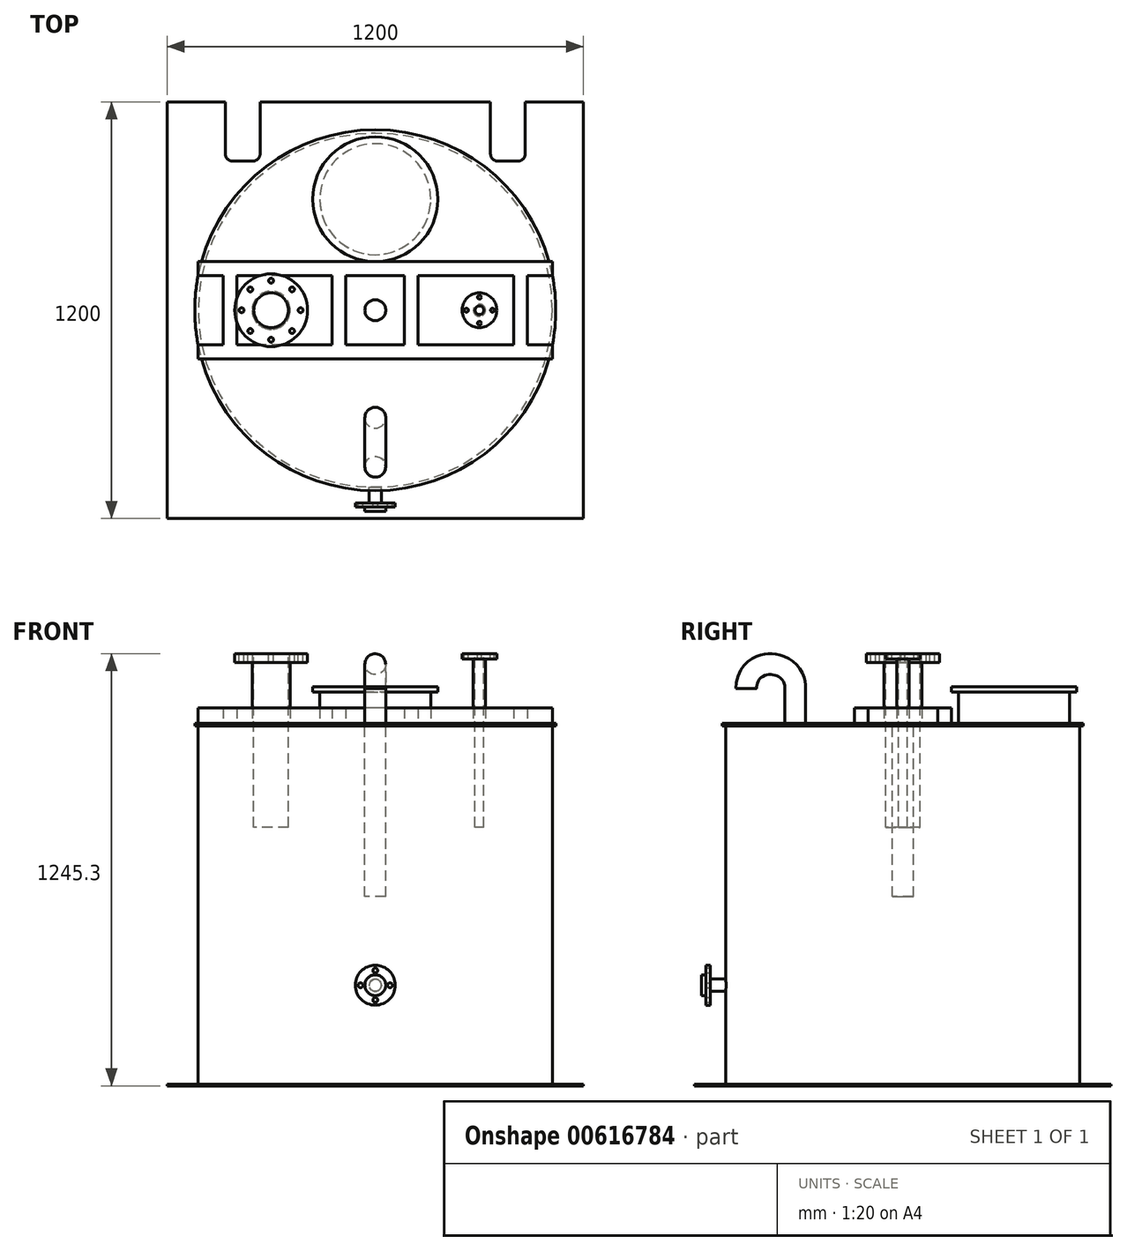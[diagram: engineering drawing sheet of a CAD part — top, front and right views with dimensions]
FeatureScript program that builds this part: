
annotation { "Feature Type Name" : "Feature", "Feature Type Description" : "" }
export const myFeature = defineFeature(function(context is Context, id is Id, definition is map)
    precondition{}
    {
        {
            var Q0;
            Q0=qCreatedBy(makeId("Front.planeOp"),FACE);
            var sketch = newSketch(context, id + "F0", { "sketchPlane" : qUnion([Q0])});
            skLineSegment(sketch, "E0.bottom", {"start": v(0, 0) * mm, "end": v(510, 0) * mm});
            skLineSegment(sketch, "E0.top", {"start": v(0, 1040) * mm, "end": v(510, 1040) * mm});
            skLineSegment(sketch, "E0.left", {"start": v(0, 0) * mm, "end": v(0, 1040) * mm});
            skLineSegment(sketch, "E0.right", {"start": v(510, 0) * mm, "end": v(510, 1032) * mm});
            skLineSegment(sketch, "E1.bottom", {"start": v(510, 1040) * mm, "end": v(520, 1040) * mm});
            skLineSegment(sketch, "E1.top", {"start": v(510, 1032) * mm, "end": v(520, 1032) * mm});
            skLineSegment(sketch, "E1.right", {"start": v(520, 1040) * mm, "end": v(520, 1032) * mm});
            skSolve(sketch);
        }
        {
            var Q0;
            Q0=makeQuery(id+"F0.imprint","IMPRINT",FACE,{"disambiguationData":[TD([[makeQuery(id+"F0.imprint","IMPRINT",EDGE,{"derivedFrom":sQuery(id+"F0.wireOp",EDGE,"E0.bottom")}),1.0]])]});
            var Q1;
            Q1=sQuery(id+"F0.wireOp",EDGE,"E0.left");
            revolve(context, id + "F1", {"entities" : qUnion([Q0]), "axis" : qUnion([Q1]), "revolveType" : RevolveType.FULL});
        }
        {
            var Q0;
            Q0=makeQuery(id+"F1.opRevolve","SWEPT_FACE",FACE,{"disambiguationData":[OSD([sQuery(id+"F0.wireOp",EDGE,"E0.bottom")])]});
            var sketch = newSketch(context, id + "F2", { "sketchPlane" : qUnion([Q0])});
            skLineSegment(sketch, "E2.bottom", {"start": v(600, -600) * mm, "end": v(432, -600) * mm});
            skLineSegment(sketch, "E2.top", {"start": v(600, 600) * mm, "end": v(-600, 600) * mm});
            skLineSegment(sketch, "E2.left", {"start": v(600, -600) * mm, "end": v(600, 600) * mm});
            skLineSegment(sketch, "E2.right", {"start": v(-600, -600) * mm, "end": v(-600, 600) * mm});
            skPoint(sketch, "E2.middle", {"position": v(0, 0) * mm});
            skLineSegment(sketch, "E3.top", {"start": v(412, -430) * mm, "end": v(352, -430) * mm});
            skLineSegment(sketch, "E3.left", {"start": v(332, -600) * mm, "end": v(332, -450) * mm});
            skLineSegment(sketch, "E3.right", {"start": v(432, -600) * mm, "end": v(432, -450) * mm});
            skLineSegment(sketch, "E4.top", {"start": v(-352, -430) * mm, "end": v(-412, -430) * mm});
            skLineSegment(sketch, "E4.left", {"start": v(-332, -600) * mm, "end": v(-332, -450) * mm});
            skLineSegment(sketch, "E4.right", {"start": v(-432, -600) * mm, "end": v(-432, -450) * mm});
            skPoint(sketch, "E5.visualSharp", {"position": v(-432, -430) * mm});
            skArc(sketch, "E5.filletArc", {"start": v(-412, -430) * mm, "mid": v(-426.14, -435.86) * mm, "end": v(-432, -450) * mm});
            skPoint(sketch, "E6.visualSharp", {"position": v(-332, -430) * mm});
            skArc(sketch, "E6.filletArc", {"start": v(-332, -450) * mm, "mid": v(-337.86, -435.86) * mm, "end": v(-352, -430) * mm});
            skPoint(sketch, "E7.visualSharp", {"position": v(332, -430) * mm});
            skArc(sketch, "E7.filletArc", {"start": v(352, -430) * mm, "mid": v(337.86, -435.86) * mm, "end": v(332, -450) * mm});
            skPoint(sketch, "E8.visualSharp", {"position": v(432, -430) * mm});
            skArc(sketch, "E8.filletArc", {"start": v(432, -450) * mm, "mid": v(426.14, -435.86) * mm, "end": v(412, -430) * mm});
            skLineSegment(sketch, "E9.trimOffspring", {"start": v(332, -600) * mm, "end": v(-332, -600) * mm});
            skLineSegment(sketch, "E10.trimOffspring", {"start": v(-432, -600) * mm, "end": v(-600, -600) * mm});
            skSolve(sketch);
        }
        {
            var Q0;
            Q0 = qSketchRegion(id + "F2", true);
            extrude(context, id + "F3", {"entities" : qUnion([Q0]), "operationType" : NewBodyOperationType.ADD, "depth" : 5 * mm, "offsetDistance" : 25 * mm});
        }
        {
            var Q0;
            Q0=qCreatedBy(makeId("Front.planeOp"),FACE);
            var sketch = newSketch(context, id + "F4", { "sketchPlane" : qUnion([Q0])});
            skCircle(sketch, "E11", {"center": v(0, 285) * mm, "radius": 17.5 * mm});
            skSolve(sketch);
        }
        {
            var Q0;
            Q0 = qSketchRegion(id + "F4", true);
            extrude(context, id + "F5", {"entities" : qUnion([Q0]), "operationType" : NewBodyOperationType.ADD, "depth" : 580 * mm, "offsetDistance" : 25 * mm});
        }
        {
            var Q0;
            Q0=makeQuery(id+"F5.opExtrude","CAP_FACE",FACE,{"disambiguationData":[OSD([sQuery(id+"F4.wireOp",EDGE,"E11")])],"isStart":false});
            cPlane(context, id + "F6", {"entities" : qUnion([Q0]), "cplaneType" : CPlaneType.OFFSET, "offset" : 25 * mm, "oppositeDirection" : true, "width" : 150 * mm, "height" : 150 * mm});
        }
        {
            var Q0;
            Q0=qCreatedBy(id+"F6.planeOp",FACE);
            var sketch = newSketch(context, id + "F7", { "sketchPlane" : qUnion([Q0])});
            skCircle(sketch, "E12", {"center": v(0, 285) * mm, "radius": 57.5 * mm});
            skCircle(sketch, "E13", {"center": v(0, 327.5) * mm, "radius": 7 * mm});
            skCircle(sketch, "E14.1.0", {"center": v(-42.5, 285) * mm, "radius": 7 * mm});
            skCircle(sketch, "E14.2.0", {"center": v(0, 242.5) * mm, "radius": 7 * mm});
            skCircle(sketch, "E14.3.0", {"center": v(42.5, 285) * mm, "radius": 7 * mm});
            skSolve(sketch);
        }
        {
            var Q0;
            Q0 = qSketchRegion(id + "F7", true);
            extrude(context, id + "F8", {"entities" : qUnion([Q0]), "operationType" : NewBodyOperationType.ADD, "depth" : 12 * mm, "offsetDistance" : 25 * mm});
        }
        {
            var Q0;
            Q0=makeQuery(id+"F8.opExtrude","CAP_FACE",FACE,{"disambiguationData":[OSD([sQuery(id+"F7.wireOp",EDGE,"E12"),sQuery(id+"F7.wireOp",EDGE,"E13"),sQuery(id+"F7.wireOp",EDGE,"E14.1.0"),sQuery(id+"F7.wireOp",EDGE,"E14.2.0"),sQuery(id+"F7.wireOp",EDGE,"E14.3.0")])],"isStart":false});
            var sketch = newSketch(context, id + "F9", { "sketchPlane" : qUnion([Q0])});
            skCircle(sketch, "E15", {"center": v(0, 285) * mm, "radius": 30 * mm});
            skSolve(sketch);
        }
        {
            var Q0;
            Q0 = qSketchRegion(id + "F9", true);
            extrude(context, id + "F10", {"entities" : qUnion([Q0]), "operationType" : NewBodyOperationType.ADD, "depth" : 13 * mm, "offsetDistance" : 25 * mm});
        }
        {
            var Q0;
            Q0=makeQuery(id+"F1.opRevolve","SWEPT_FACE",FACE,{"disambiguationData":[OSD([sQuery(id+"F0.wireOp",EDGE,"E0.top"),sQuery(id+"F0.wireOp",EDGE,"E1.bottom")])]});
            var sketch = newSketch(context, id + "F11", { "sketchPlane" : qUnion([Q0])});
            skLineSegment(sketch, "E16.bottom", {"start": v(510.5, 140) * mm, "end": v(-510.5, 140) * mm});
            skLineSegment(sketch, "E16.top", {"start": v(510.5, 100) * mm, "end": v(438.5, 100) * mm});
            skLineSegment(sketch, "E16.left", {"start": v(510.5, 140) * mm, "end": v(510.5, 100) * mm});
            skLineSegment(sketch, "E16.right", {"start": v(-510.5, 140) * mm, "end": v(-510.5, 100) * mm});
            skLineSegment(sketch, "E17.bottom", {"start": v(510.5, -100) * mm, "end": v(438.5, -100) * mm});
            skLineSegment(sketch, "E17.top", {"start": v(510.5, -140) * mm, "end": v(-510.5, -140) * mm});
            skLineSegment(sketch, "E17.left", {"start": v(510.5, -100) * mm, "end": v(510.5, -140) * mm});
            skLineSegment(sketch, "E17.right", {"start": v(-510.5, -100) * mm, "end": v(-510.5, -140) * mm});
            skLineSegment(sketch, "E18.left", {"start": v(438.5, 100) * mm, "end": v(438.5, -100) * mm});
            skLineSegment(sketch, "E18.right", {"start": v(398.5, 100) * mm, "end": v(398.5, -100) * mm});
            skLineSegment(sketch, "E19.left", {"start": v(123.5, 100) * mm, "end": v(123.5, -100) * mm});
            skLineSegment(sketch, "E19.right", {"start": v(83.5, 100) * mm, "end": v(83.5, -100) * mm});
            skLineSegment(sketch, "E20.left", {"start": v(-85, 100) * mm, "end": v(-85, -100) * mm});
            skLineSegment(sketch, "E20.right", {"start": v(-125, 100) * mm, "end": v(-125, -100) * mm});
            skLineSegment(sketch, "E21.left", {"start": v(-398.5, 100) * mm, "end": v(-398.5, -100) * mm});
            skLineSegment(sketch, "E21.right", {"start": v(-438.5, 100) * mm, "end": v(-438.5, -100) * mm});
            skLineSegment(sketch, "E22.trimOffspring", {"start": v(398.5, 100) * mm, "end": v(123.5, 100) * mm});
            skLineSegment(sketch, "E23.trimOffspring", {"start": v(83.5, 100) * mm, "end": v(-85, 100) * mm});
            skLineSegment(sketch, "E24.trimOffspring", {"start": v(83.5, -100) * mm, "end": v(-85, -100) * mm});
            skLineSegment(sketch, "E25.trimOffspring", {"start": v(-125, -100) * mm, "end": v(-398.5, -100) * mm});
            skLineSegment(sketch, "E26.trimOffspring", {"start": v(-125, 100) * mm, "end": v(-398.5, 100) * mm});
            skLineSegment(sketch, "E27.trimOffspring", {"start": v(-438.5, 100) * mm, "end": v(-510.5, 100) * mm});
            skLineSegment(sketch, "E28.trimOffspring", {"start": v(-438.5, -100) * mm, "end": v(-510.5, -100) * mm});
            skLineSegment(sketch, "E29", {"start": v(398.5, -100) * mm, "end": v(123.5, -100) * mm});
            skSolve(sketch);
        }
        {
            var Q0;
            Q0 = qSketchRegion(id + "F11", true);
            extrude(context, id + "F12", {"entities" : qUnion([Q0]), "operationType" : NewBodyOperationType.ADD, "depth" : 44 * mm, "offsetDistance" : 25 * mm});
        }
        {
            var Q0;
            {var subQ0=sQuery(id+"F11.wireOp",EDGE,"E16.bottom");Q0=makeQuery(id+"F12.boolean.opBoolean","SPLIT",FACE,{"disambiguationData":[TD([makeQuery(id+"F12.opExtrude","SWEPT_FACE",FACE,{"disambiguationData":[OSD([subQ0])]})])],"derivedFrom":makeQuery(id+"F1.opRevolve","SWEPT_FACE",FACE,{"disambiguationData":[OSD([sQuery(id+"F0.wireOp",EDGE,"E0.top"),sQuery(id+"F0.wireOp",EDGE,"E1.bottom")])]})});}
            var sketch = newSketch(context, id + "F13", { "sketchPlane" : qUnion([Q0])});
            skCircle(sketch, "E30", {"center": v(0, 320) * mm, "radius": 160 * mm});
            skSolve(sketch);
        }
        {
            var Q0;
            Q0=makeQuery(id+"F13.imprint","IMPRINT",FACE,{"disambiguationData":[TD([[makeQuery(id+"F13.imprint","IMPRINT",EDGE,{"derivedFrom":sQuery(id+"F13.wireOp",EDGE,"E30")}),1.0]])]});
            extrude(context, id + "F14", {"entities" : qUnion([Q0]), "operationType" : NewBodyOperationType.ADD, "depth" : 90 * mm, "offsetDistance" : 25 * mm});
        }
        {
            var Q0;
            Q0=makeQuery(id+"F14.opExtrude","CAP_FACE",FACE,{"disambiguationData":[OSD([sQuery(id+"F13.wireOp",EDGE,"E30")])],"isStart":false});
            var sketch = newSketch(context, id + "F15", { "sketchPlane" : qUnion([Q0])});
            skCircle(sketch, "E31", {"center": v(0, 320) * mm, "radius": 180 * mm});
            skSolve(sketch);
        }
        {
            var Q0;
            Q0 = qSketchRegion(id + "F15", true);
            extrude(context, id + "F16", {"entities" : qUnion([Q0]), "operationType" : NewBodyOperationType.ADD, "depth" : 15 * mm, "offsetDistance" : 25 * mm});
        }
        {
            var Q0;
            Q0=makeQuery(id+"F12.boolean.opBoolean","SPLIT",FACE,{"disambiguationData":[TD([makeQuery(id+"F12.opExtrude","SWEPT_FACE",FACE,{"disambiguationData":[OSD([sQuery(id+"F11.wireOp",EDGE,"E19.right")])]})])],"derivedFrom":makeQuery(id+"F1.opRevolve","SWEPT_FACE",FACE,{"disambiguationData":[OSD([sQuery(id+"F0.wireOp",EDGE,"E0.top"),sQuery(id+"F0.wireOp",EDGE,"E1.bottom")])]})});
            var sketch = newSketch(context, id + "F17", { "sketchPlane" : qUnion([Q0])});
            skCircle(sketch, "E32", {"center": v(0, 0) * mm, "radius": 30 * mm});
            skSolve(sketch);
        }
        {
            var Q0;
            Q0=makeQuery(id+"F17.imprint","IMPRINT",FACE,{"disambiguationData":[TD([[makeQuery(id+"F17.imprint","IMPRINT",EDGE,{"derivedFrom":sQuery(id+"F17.wireOp",EDGE,"E32")}),1.0]])]});
            extrude(context, id + "F18", {"entities" : qUnion([Q0]), "operationType" : NewBodyOperationType.REMOVE, "oppositeDirection" : true, "depth" : 500 * mm, "offsetDistance" : 25 * mm});
        }
        {
            var Q0;
            {var subQ0=sQuery(id+"F11.wireOp",EDGE,"E17.top");Q0=makeQuery(id+"F12.boolean.opBoolean","SPLIT",FACE,{"disambiguationData":[TD([makeQuery(id+"F12.opExtrude","SWEPT_FACE",FACE,{"disambiguationData":[OSD([subQ0])]})])],"derivedFrom":makeQuery(id+"F1.opRevolve","SWEPT_FACE",FACE,{"disambiguationData":[OSD([sQuery(id+"F0.wireOp",EDGE,"E0.top"),sQuery(id+"F0.wireOp",EDGE,"E1.bottom")])]})});}
            var sketch = newSketch(context, id + "F19", { "sketchPlane" : qUnion([Q0])});
            skCircle(sketch, "E33", {"center": v(0, -310) * mm, "radius": 30 * mm});
            skSolve(sketch);
        }
        {
            var Q0;
            Q0=qCreatedBy(makeId("Right.planeOp"),FACE);
            var sketch = newSketch(context, id + "F20", { "sketchPlane" : qUnion([Q0])});
            skPoint(sketch, "E34.0", {"position": v(-310, 1040) * mm});
            skLineSegment(sketch, "E35", {"start": v(-310, 1040) * mm, "end": v(-310, 1140) * mm});
            skFitSpline(sketch, "E36", {"points": [v(-310, 1140) * mm, v(-451.09, 1140) * mm], "startDerivative": vector(-1.84, 276.58) * mm, "endDerivative": vector(1.84, -285.78) * mm});
            skSolve(sketch);
        }
        {
            var Q0;
            Q0=makeQuery(id+"F19.imprint","IMPRINT",FACE,{"disambiguationData":[TD([[makeQuery(id+"F19.imprint","IMPRINT",EDGE,{"derivedFrom":sQuery(id+"F19.wireOp",EDGE,"E33")}),1.0]])]});
            var Q1;
            Q1=sQuery(id+"F20.wireOp",EDGE,"E35");
            var Q2;
            Q2=sQuery(id+"F20.wireOp",EDGE,"E36");
            sweep(context, id + "F21", {"operationType" : NewBodyOperationType.ADD, "profiles" : qUnion([Q0]), "path" : qUnion([Q1, Q2])});
        }
        {
            var Q0;
            Q0=makeQuery(id+"F12.boolean.opBoolean","SPLIT",FACE,{"disambiguationData":[TD([makeQuery(id+"F12.opExtrude","SWEPT_FACE",FACE,{"disambiguationData":[OSD([sQuery(id+"F11.wireOp",EDGE,"E20.right")])]})])],"derivedFrom":makeQuery(id+"F1.opRevolve","SWEPT_FACE",FACE,{"disambiguationData":[OSD([sQuery(id+"F0.wireOp",EDGE,"E0.top"),sQuery(id+"F0.wireOp",EDGE,"E1.bottom")])]})});
            var sketch = newSketch(context, id + "F22", { "sketchPlane" : qUnion([Q0])});
            skCircle(sketch, "E37", {"center": v(300, 0) * mm, "radius": 17.5 * mm});
            skCircle(sketch, "E38", {"center": v(-300, 0) * mm, "radius": 55 * mm});
            skSolve(sketch);
        }
        {
            var Q0;
            Q0 = qSketchRegion(id + "F22", true);
            extrude(context, id + "F23", {"entities" : qUnion([Q0]), "operationType" : NewBodyOperationType.ADD, "depth" : 200 * mm, "offsetDistance" : 25 * mm});
        }
        {
            var Q0;
            Q0=makeQuery(id+"F23.opExtrude","CAP_FACE",FACE,{"disambiguationData":[OSD([sQuery(id+"F22.wireOp",EDGE,"E38")])],"isStart":false});
            var sketch = newSketch(context, id + "F24", { "sketchPlane" : qUnion([Q0])});
            skCircle(sketch, "E39", {"center": v(-300, 0) * mm, "radius": 105 * mm});
            skCircle(sketch, "E40", {"center": v(-215, 0) * mm, "radius": 7 * mm});
            skCircle(sketch, "E41.1.0", {"center": v(-239.9, 60.1) * mm, "radius": 7 * mm});
            skCircle(sketch, "E41.2.0", {"center": v(-300, 85) * mm, "radius": 7 * mm});
            skCircle(sketch, "E41.3.0", {"center": v(-360.1, 60.1) * mm, "radius": 7 * mm});
            skCircle(sketch, "E41.4.0", {"center": v(-385, 0) * mm, "radius": 7 * mm});
            skCircle(sketch, "E41.5.0", {"center": v(-360.1, -60.1) * mm, "radius": 7 * mm});
            skCircle(sketch, "E41.6.0", {"center": v(-300, -85) * mm, "radius": 7 * mm});
            skCircle(sketch, "E41.7.0", {"center": v(-239.9, -60.1) * mm, "radius": 7 * mm});
            skSolve(sketch);
        }
        {
            var Q0;
            Q0 = qSketchRegion(id + "F24", true);
            extrude(context, id + "F25", {"entities" : qUnion([Q0]), "operationType" : NewBodyOperationType.ADD, "oppositeDirection" : true, "depth" : 25 * mm, "offsetDistance" : 25 * mm});
        }
        {
            var Q0;
            Q0=makeQuery(id+"F25.boolean.opBoolean","MERGE",FACE,{"derivedFrom":[makeQuery(id+"F23.opExtrude","CAP_FACE",FACE,{"disambiguationData":[OSD([sQuery(id+"F22.wireOp",EDGE,"E38")])],"isStart":false}),makeQuery(id+"F25.opExtrude","CAP_FACE",FACE,{"disambiguationData":[OSD([sQuery(id+"F24.wireOp",EDGE,"E39"),sQuery(id+"F24.wireOp",EDGE,"E40"),sQuery(id+"F24.wireOp",EDGE,"E41.1.0"),sQuery(id+"F24.wireOp",EDGE,"E41.2.0"),sQuery(id+"F24.wireOp",EDGE,"E41.3.0"),sQuery(id+"F24.wireOp",EDGE,"E41.4.0"),sQuery(id+"F24.wireOp",EDGE,"E41.5.0"),sQuery(id+"F24.wireOp",EDGE,"E41.6.0"),sQuery(id+"F24.wireOp",EDGE,"E41.7.0")])],"isStart":true})]});
            var sketch = newSketch(context, id + "F26", { "sketchPlane" : qUnion([Q0])});
            skCircle(sketch, "E42", {"center": v(-300, 0) * mm, "radius": 50 * mm});
            skSolve(sketch);
        }
        {
            var Q0;
            Q0=makeQuery(id+"F26.imprint","IMPRINT",FACE,{"disambiguationData":[TD([[makeQuery(id+"F26.imprint","IMPRINT",EDGE,{"derivedFrom":sQuery(id+"F26.wireOp",EDGE,"E42")}),1.0]])]});
            extrude(context, id + "F27", {"entities" : qUnion([Q0]), "operationType" : NewBodyOperationType.REMOVE, "oppositeDirection" : true, "depth" : 500 * mm, "offsetDistance" : 25 * mm});
        }
        {
            var Q0;
            Q0=makeQuery(id+"F23.opExtrude","CAP_FACE",FACE,{"disambiguationData":[OSD([sQuery(id+"F22.wireOp",EDGE,"E37")])],"isStart":false});
            var sketch = newSketch(context, id + "F28", { "sketchPlane" : qUnion([Q0])});
            skCircle(sketch, "E43", {"center": v(300, 0) * mm, "radius": 50 * mm});
            skSolve(sketch);
        }
        {
            var Q0;
            Q0 = qSketchRegion(id + "F28", true);
            extrude(context, id + "F29", {"entities" : qUnion([Q0]), "operationType" : NewBodyOperationType.ADD, "oppositeDirection" : true, "depth" : 15 * mm, "offsetDistance" : 25 * mm});
        }
        {
            var Q0;
            Q0=makeQuery(id+"F29.boolean.opBoolean","MERGE",FACE,{"derivedFrom":[makeQuery(id+"F23.opExtrude","CAP_FACE",FACE,{"disambiguationData":[OSD([sQuery(id+"F22.wireOp",EDGE,"E37")])],"isStart":false}),makeQuery(id+"F29.opExtrude","CAP_FACE",FACE,{"disambiguationData":[OSD([sQuery(id+"F28.wireOp",EDGE,"E43")])],"isStart":true})]});
            var sketch = newSketch(context, id + "F30", { "sketchPlane" : qUnion([Q0])});
            skCircle(sketch, "E44", {"center": v(337.5, 0) * mm, "radius": 5.5 * mm});
            skCircle(sketch, "E45.1.0", {"center": v(300, 37.5) * mm, "radius": 5.5 * mm});
            skCircle(sketch, "E45.2.0", {"center": v(262.5, 0) * mm, "radius": 5.5 * mm});
            skCircle(sketch, "E45.3.0", {"center": v(300, -37.5) * mm, "radius": 5.5 * mm});
            skPoint(sketch, "E45.center", {"position": v(300, 0) * mm});
            skSolve(sketch);
        }
        {
            var Q0;
            Q0 = qSketchRegion(id + "F30", true);
            extrude(context, id + "F31", {"entities" : qUnion([Q0]), "operationType" : NewBodyOperationType.REMOVE, "oppositeDirection" : true, "depth" : 25 * mm, "offsetDistance" : 25 * mm});
        }
        {
            var Q0;
            Q0=makeQuery(id+"F29.boolean.opBoolean","MERGE",FACE,{"derivedFrom":[makeQuery(id+"F23.opExtrude","CAP_FACE",FACE,{"disambiguationData":[OSD([sQuery(id+"F22.wireOp",EDGE,"E37")])],"isStart":false}),makeQuery(id+"F29.opExtrude","CAP_FACE",FACE,{"disambiguationData":[OSD([sQuery(id+"F28.wireOp",EDGE,"E43")])],"isStart":true})]});
            var sketch = newSketch(context, id + "F32", { "sketchPlane" : qUnion([Q0])});
            skCircle(sketch, "E46", {"center": v(300, 0) * mm, "radius": 12.5 * mm});
            skSolve(sketch);
        }
        {
            var Q0;
            Q0=makeQuery(id+"F32.imprint","IMPRINT",FACE,{"disambiguationData":[TD([[makeQuery(id+"F32.imprint","IMPRINT",EDGE,{"derivedFrom":sQuery(id+"F32.wireOp",EDGE,"E46")}),1.0]])]});
            extrude(context, id + "F33", {"entities" : qUnion([Q0]), "operationType" : NewBodyOperationType.REMOVE, "oppositeDirection" : true, "depth" : 500 * mm, "offsetDistance" : 25 * mm});
        }
    });
